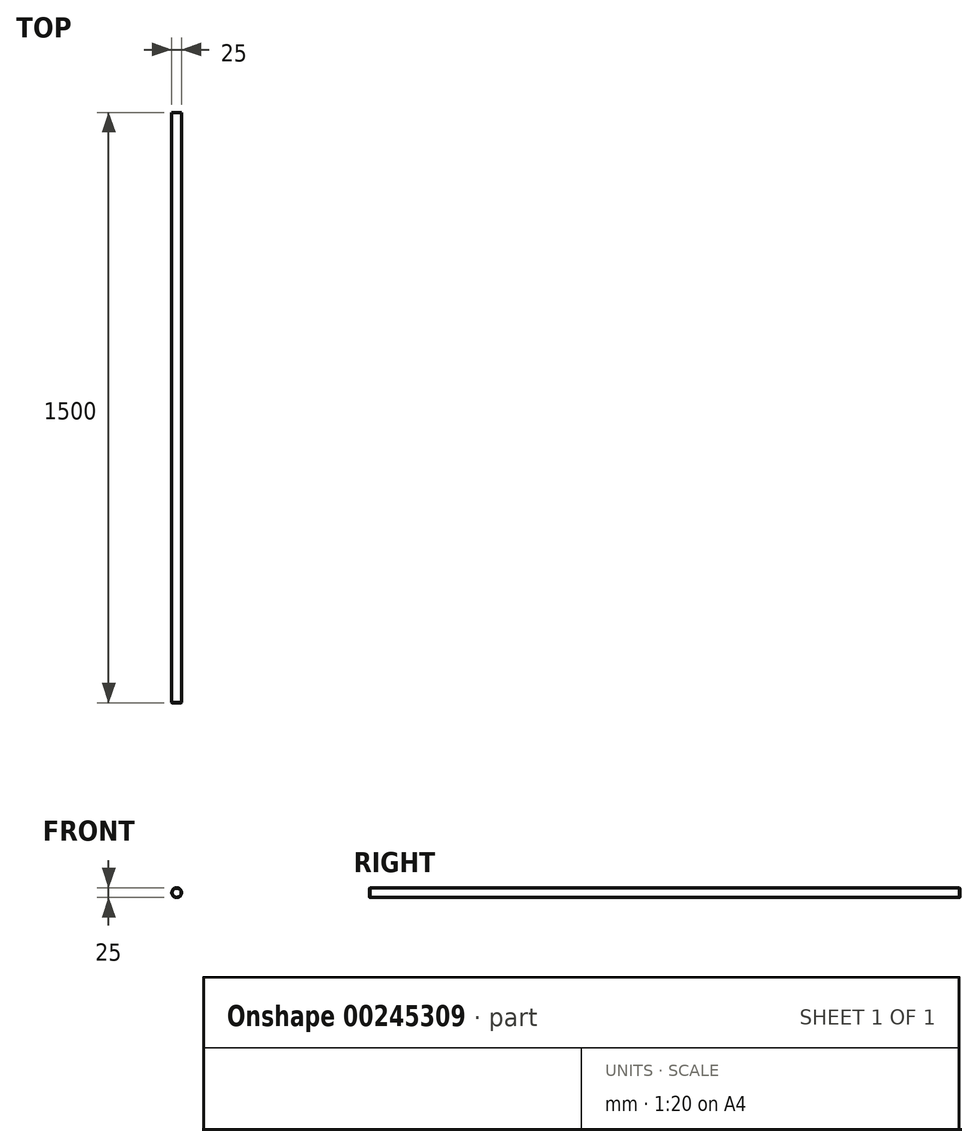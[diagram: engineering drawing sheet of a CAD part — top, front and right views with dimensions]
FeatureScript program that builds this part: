
annotation { "Feature Type Name" : "Feature", "Feature Type Description" : "" }
export const myFeature = defineFeature(function(context is Context, id is Id, definition is map)
    precondition{}
    {
        {
            var Q0;
            Q0=qCreatedBy(makeId("Front.planeOp"),FACE);
            var sketch = newSketch(context, id + "F0", { "sketchPlane" : qUnion([Q0])});
            skCircle(sketch, "E0", {"center": v(0, 0) * mm, "radius": 12.5 * mm});
            skSolve(sketch);
        }
        {
            var Q0;
            Q0=makeQuery(id+"F0.imprint","IMPRINT",FACE,{"disambiguationData":[TD([[makeQuery(id+"F0.imprint","IMPRINT",EDGE,{"derivedFrom":sQuery(id+"F0.wireOp",EDGE,"E0")}),1.0]])]});
            extrude(context, id + "F1", {"entities" : qUnion([Q0]), "depth" : 1500 * mm, "offsetDistance" : 25 * mm});
        }
        {
            var Q0;
            Q0=makeQuery(id+"F1.opExtrude","CAP_EDGE",EDGE,{"disambiguationData":[OSD([sQuery(id+"F0.wireOp",EDGE,"E0")])],"isStart":false});
            var Q1;
            Q1=makeQuery(id+"F1.opExtrude","CAP_EDGE",EDGE,{"disambiguationData":[OSD([sQuery(id+"F0.wireOp",EDGE,"E0")])],"isStart":true});
            chamfer(context, id + "F2", {"entities" : qUnion([Q0, Q1]), "width" : 1 * mm, "tangentPropagation" : true});
        }
    });
